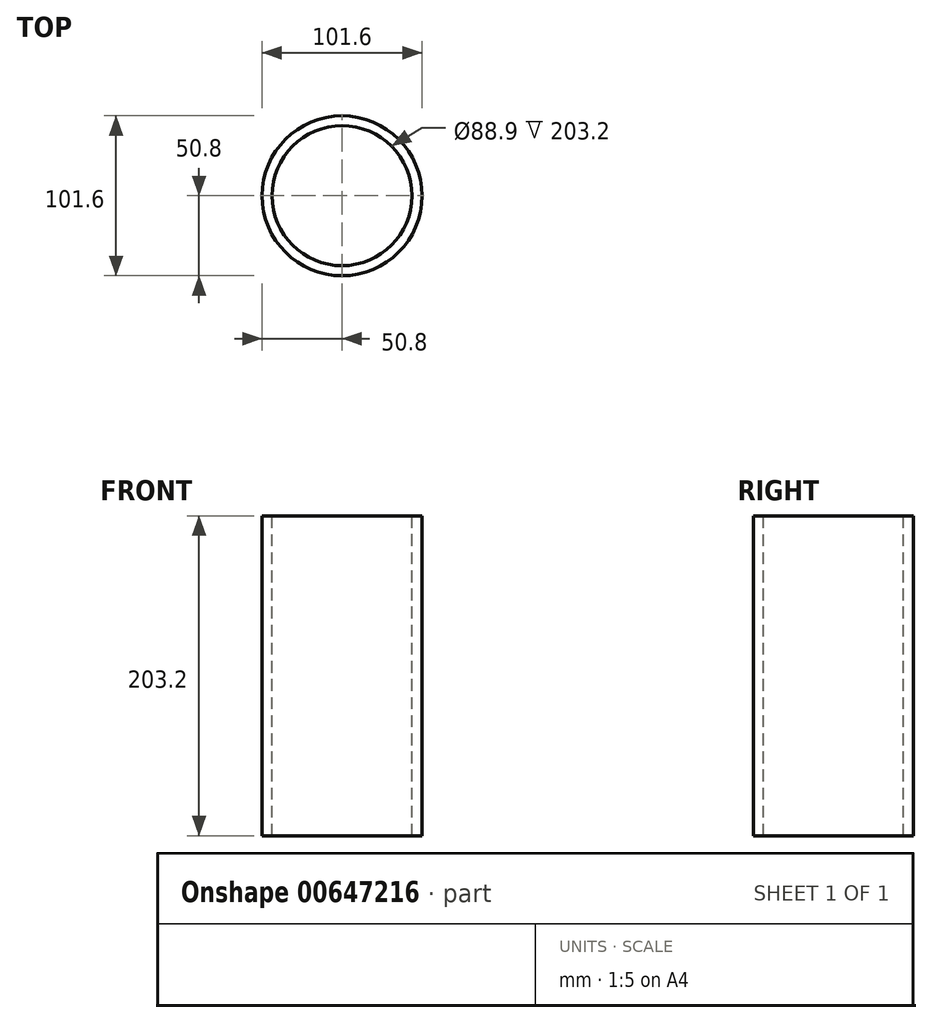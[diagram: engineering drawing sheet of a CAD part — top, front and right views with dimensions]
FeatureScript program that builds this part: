
annotation { "Feature Type Name" : "Feature", "Feature Type Description" : "" }
export const myFeature = defineFeature(function(context is Context, id is Id, definition is map)
    precondition{}
    {
        {
            var Q0;
            Q0=qCreatedBy(makeId("Right.planeOp"),FACE);
            var sketch = newSketch(context, id + "F0", { "sketchPlane" : qUnion([Q0])});
            skLineSegment(sketch, "E0.bottom", {"start": v(50.8, -75.65) * mm, "end": v(44.45, -75.65) * mm});
            skLineSegment(sketch, "E0.top", {"start": v(50.8, 76.75) * mm, "end": v(44.45, 76.75) * mm});
            skLineSegment(sketch, "E0.left", {"start": v(50.8, -75.65) * mm, "end": v(50.8, 76.75) * mm});
            skLineSegment(sketch, "E0.right", {"start": v(44.45, -75.65) * mm, "end": v(44.45, 76.75) * mm});
            skLineSegment(sketch, "E1.MirrorCS", {"start": v(-50.8, -75.65) * mm, "end": v(-50.8, 76.75) * mm});
            skLineSegment(sketch, "E2.MirrorCS", {"start": v(-50.8, -75.65) * mm, "end": v(-44.45, -75.65) * mm});
            skLineSegment(sketch, "E3.MirrorCS", {"start": v(-44.45, -75.65) * mm, "end": v(-44.45, 76.75) * mm});
            skLineSegment(sketch, "E4.MirrorCS", {"start": v(-50.8, 76.75) * mm, "end": v(-44.45, 76.75) * mm});
            skLineSegment(sketch, "E5", {"start": v(0, 77.92) * mm, "end": v(0, -76.68) * mm});
            skSolve(sketch);
        }
        {
            var Q0;
            Q0=makeQuery(id+"F0.imprint","IMPRINT",FACE,{"disambiguationData":[TD([[makeQuery(id+"F0.imprint","IMPRINT",EDGE,{"derivedFrom":sQuery(id+"F0.wireOp",EDGE,"E1.MirrorCS")}),-1.0]])]});
            var Q1;
            Q1=sQuery(id+"F0.wireOp",EDGE,"E5");
            revolve(context, id + "F1", {"entities" : qUnion([Q0]), "axis" : qUnion([Q1]), "revolveType" : RevolveType.FULL});
        }
        {
            var Q0;
            Q0=makeQuery(id+"F1.opRevolve","SWEPT_FACE",FACE,{"disambiguationData":[OSD([sQuery(id+"F0.wireOp",EDGE,"E4.MirrorCS")])]});
            var sketch = newSketch(context, id + "F2", { "sketchPlane" : qUnion([Q0])});
            skPoint(sketch, "E6", {"position": v(-44.45, 0) * mm});
            skSolve(sketch);
        }
        {
            var Q0;
            Q0 = qSketchRegion(id + "F2", true);
            var Q1;
            {var subQ0=sQuery(id+"F0.wireOp",EDGE,"E4.MirrorCS");Q1=makeQuery(id+"F2.imprint","IMPRINT",FACE,{"disambiguationData":[TD([[makeQuery(id+"F2.imprint","IMPRINT",EDGE,{"derivedFrom":makeQuery(id+"F1.opRevolve","SWEPT_EDGE",EDGE,{"disambiguationData":[OSD([sQuery(id+"F0.wireOp",EDGE,"E1.MirrorCS"),subQ0])]})}),1.0]])]});}
            extrude(context, id + "F3", {"entities" : qUnion([Q0, Q1]), "operationType" : NewBodyOperationType.ADD, "depth" : 50.8 * mm, "offsetDistance" : 25.4 * mm});
        }
    });
